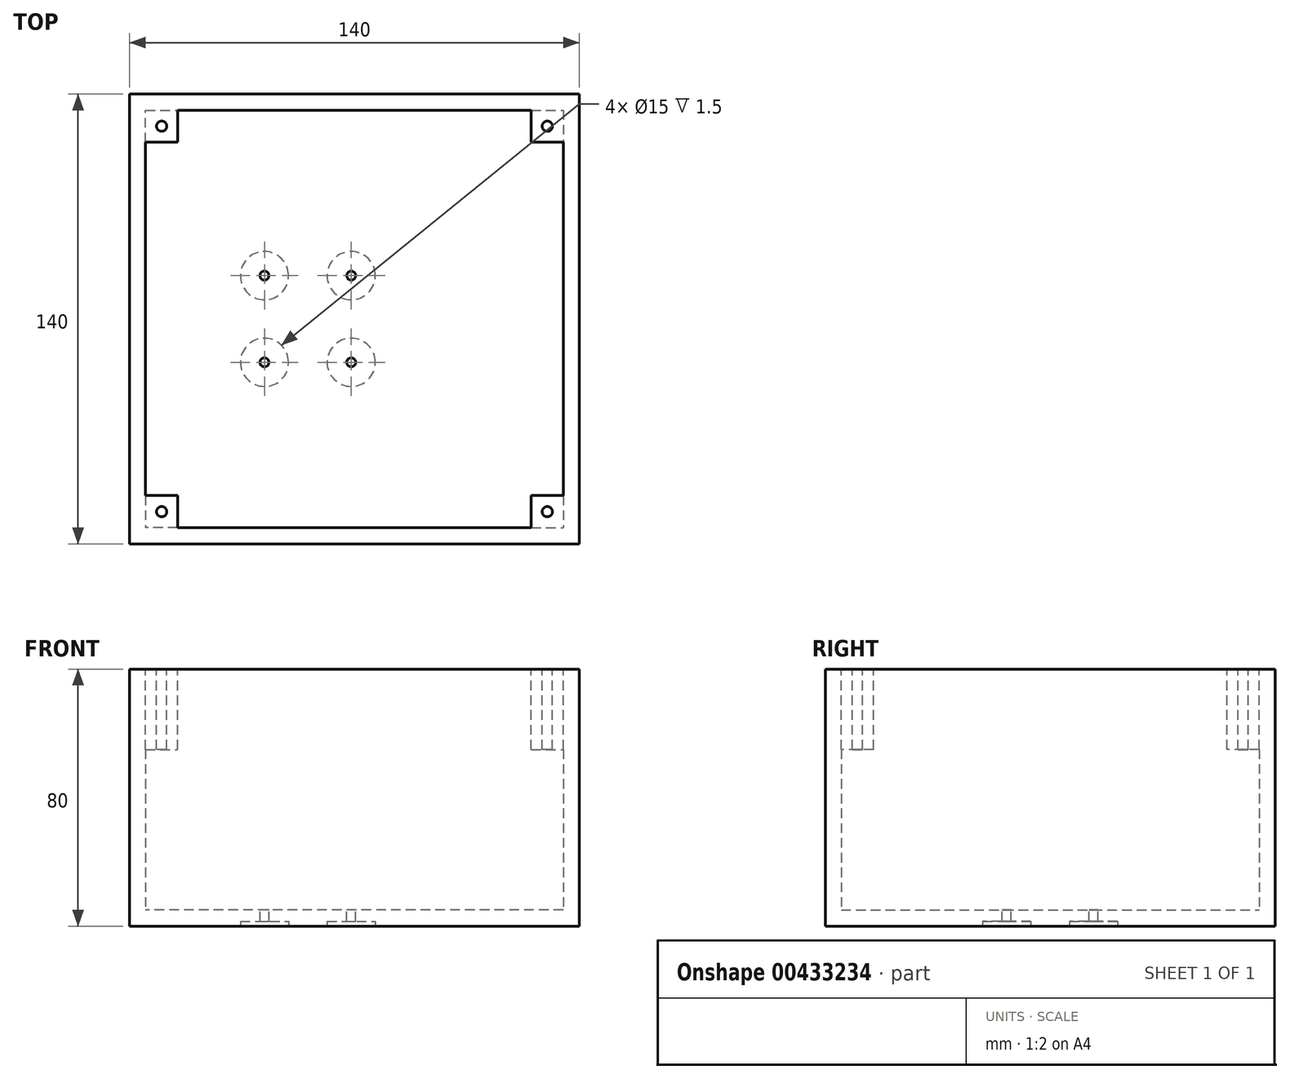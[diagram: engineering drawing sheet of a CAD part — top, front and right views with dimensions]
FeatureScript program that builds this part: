
annotation { "Feature Type Name" : "Feature", "Feature Type Description" : "" }
export const myFeature = defineFeature(function(context is Context, id is Id, definition is map)
    precondition{}
    {
        {
            var Q0;
            Q0=qCreatedBy(makeId("Top.planeOp"),FACE);
            var sketch = newSketch(context, id + "F0", { "sketchPlane" : qUnion([Q0])});
            skLineSegment(sketch, "E0.bottom", {"start": v(-70, 70) * mm, "end": v(70, 70) * mm});
            skLineSegment(sketch, "E0.top", {"start": v(-70, -70) * mm, "end": v(70, -70) * mm});
            skLineSegment(sketch, "E0.left", {"start": v(-70, 70) * mm, "end": v(-70, -70) * mm});
            skLineSegment(sketch, "E0.right", {"start": v(70, 70) * mm, "end": v(70, -70) * mm});
            skPoint(sketch, "E0.middle", {"position": v(0, 0) * mm});
            skLineSegment(sketch, "E1.bottom", {"start": v(-65, 65) * mm, "end": v(65, 65) * mm});
            skLineSegment(sketch, "E1.top", {"start": v(-65, -65) * mm, "end": v(65, -65) * mm});
            skLineSegment(sketch, "E1.left", {"start": v(-65, 65) * mm, "end": v(-65, -65) * mm});
            skLineSegment(sketch, "E1.right", {"start": v(65, 65) * mm, "end": v(65, -65) * mm});
            skSolve(sketch);
        }
        {
            var Q0;
            Q0 = qSketchRegion(id + "F0", true);
            extrude(context, id + "F1", {"entities" : qUnion([Q0]), "depth" : 80 * mm});
        }
        {
            var Q0;
            Q0=makeQuery(id+"F1.opExtrude","CAP_FACE",FACE,{"disambiguationData":[OSD([sQuery(id+"F0.wireOp",EDGE,"E0.bottom"),sQuery(id+"F0.wireOp",EDGE,"E0.top"),sQuery(id+"F0.wireOp",EDGE,"E0.left"),sQuery(id+"F0.wireOp",EDGE,"E0.right"),sQuery(id+"F0.wireOp",EDGE,"E1.bottom"),sQuery(id+"F0.wireOp",EDGE,"E1.top"),sQuery(id+"F0.wireOp",EDGE,"E1.left"),sQuery(id+"F0.wireOp",EDGE,"E1.right")])],"isStart":true});
            var sketch = newSketch(context, id + "F2", { "sketchPlane" : qUnion([Q0])});
            skLineSegment(sketch, "E2.bottom", {"start": v(-70, 70) * mm, "end": v(70, 70) * mm});
            skLineSegment(sketch, "E2.top", {"start": v(-70, -70) * mm, "end": v(70, -70) * mm});
            skLineSegment(sketch, "E2.left", {"start": v(-70, 70) * mm, "end": v(-70, -70) * mm});
            skLineSegment(sketch, "E2.right", {"start": v(70, 70) * mm, "end": v(70, -70) * mm});
            skSolve(sketch);
        }
        {
            var Q0;
            Q0 = qSketchRegion(id + "F2", true);
            extrude(context, id + "F3", {"entities" : qUnion([Q0]), "operationType" : NewBodyOperationType.ADD, "oppositeDirection" : true, "depth" : 5 * mm});
        }
        {
            var Q0;
            Q0=makeQuery(id+"F3.opExtrude","CAP_FACE",FACE,{"disambiguationData":[OSD([sQuery(id+"F2.wireOp",EDGE,"E2.bottom"),sQuery(id+"F2.wireOp",EDGE,"E2.top"),sQuery(id+"F2.wireOp",EDGE,"E2.left"),sQuery(id+"F2.wireOp",EDGE,"E2.right")])],"isStart":false});
            var sketch = newSketch(context, id + "F4", { "sketchPlane" : qUnion([Q0])});
            skLineSegment(sketch, "E3", {"start": v(0, 0) * mm, "end": v(-1, 0) * mm, "construction": true});
            skLineSegment(sketch, "E4", {"start": v(-1, 0) * mm, "end": v(-1, 13.5) * mm, "construction": true});
            skCircle(sketch, "E5", {"center": v(-1, 13.5) * mm, "radius": 1.4 * mm});
            skCircle(sketch, "E6", {"center": v(-28, 13.5) * mm, "radius": 1.4 * mm});
            skLineSegment(sketch, "E7", {"start": v(-2.4, 13.5) * mm, "end": v(-26.6, 13.5) * mm, "construction": true});
            skLineSegment(sketch, "E8.MirrorCS", {"start": v(-1, 0) * mm, "end": v(-1, -13.5) * mm, "construction": true});
            skCircle(sketch, "E9.MirrorC", {"center": v(-1, -13.5) * mm, "radius": 1.4 * mm});
            skLineSegment(sketch, "E10.MirrorCS", {"start": v(-2.4, -13.5) * mm, "end": v(-26.6, -13.5) * mm, "construction": true});
            skCircle(sketch, "E11.MirrorC", {"center": v(-28, -13.5) * mm, "radius": 1.4 * mm});
            skSolve(sketch);
        }
        {
            var Q0;
            Q0 = qSketchRegion(id + "F4", true);
            var Q1;
            Q1=makeQuery(id+"F3.boolean.opBoolean","MERGE",FACE,{"derivedFrom":[makeQuery(id+"F1.opExtrude","CAP_FACE",FACE,{"disambiguationData":[OSD([sQuery(id+"F0.wireOp",EDGE,"E0.bottom"),sQuery(id+"F0.wireOp",EDGE,"E0.top"),sQuery(id+"F0.wireOp",EDGE,"E0.left"),sQuery(id+"F0.wireOp",EDGE,"E0.right"),sQuery(id+"F0.wireOp",EDGE,"E1.bottom"),sQuery(id+"F0.wireOp",EDGE,"E1.top"),sQuery(id+"F0.wireOp",EDGE,"E1.left"),sQuery(id+"F0.wireOp",EDGE,"E1.right")])],"isStart":true}),makeQuery(id+"F3.opExtrude","CAP_FACE",FACE,{"disambiguationData":[OSD([sQuery(id+"F2.wireOp",EDGE,"E2.bottom"),sQuery(id+"F2.wireOp",EDGE,"E2.top"),sQuery(id+"F2.wireOp",EDGE,"E2.left"),sQuery(id+"F2.wireOp",EDGE,"E2.right")])],"isStart":true})]});
            extrude(context, id + "F5", {"entities" : qUnion([Q0]), "operationType" : NewBodyOperationType.REMOVE, "endBound" : BoundingType.UP_TO_SURFACE, "oppositeDirection" : true, "endBoundEntityFace" : qUnion([Q1]), "depth" : 25 * mm});
        }
        {
            var Q0;
            Q0=makeQuery(id+"F3.boolean.opBoolean","MERGE",FACE,{"derivedFrom":[makeQuery(id+"F1.opExtrude","CAP_FACE",FACE,{"disambiguationData":[OSD([sQuery(id+"F0.wireOp",EDGE,"E0.bottom"),sQuery(id+"F0.wireOp",EDGE,"E0.top"),sQuery(id+"F0.wireOp",EDGE,"E0.left"),sQuery(id+"F0.wireOp",EDGE,"E0.right"),sQuery(id+"F0.wireOp",EDGE,"E1.bottom"),sQuery(id+"F0.wireOp",EDGE,"E1.top"),sQuery(id+"F0.wireOp",EDGE,"E1.left"),sQuery(id+"F0.wireOp",EDGE,"E1.right")])],"isStart":true}),makeQuery(id+"F3.opExtrude","CAP_FACE",FACE,{"disambiguationData":[OSD([sQuery(id+"F2.wireOp",EDGE,"E2.bottom"),sQuery(id+"F2.wireOp",EDGE,"E2.top"),sQuery(id+"F2.wireOp",EDGE,"E2.left"),sQuery(id+"F2.wireOp",EDGE,"E2.right")])],"isStart":true})]});
            var sketch = newSketch(context, id + "F6", { "sketchPlane" : qUnion([Q0])});
            skCircle(sketch, "E12", {"center": v(-28, 13.5) * mm, "radius": 7.5 * mm});
            skCircle(sketch, "E13", {"center": v(-1, 13.5) * mm, "radius": 7.5 * mm});
            skCircle(sketch, "E14", {"center": v(-28, -13.5) * mm, "radius": 7.5 * mm});
            skCircle(sketch, "E15", {"center": v(-1, -13.5) * mm, "radius": 7.5 * mm});
            skSolve(sketch);
        }
        {
            var Q0;
            Q0 = qSketchRegion(id + "F6", true);
            extrude(context, id + "F7", {"entities" : qUnion([Q0]), "operationType" : NewBodyOperationType.REMOVE, "oppositeDirection" : true, "depth" : 1.5 * mm});
        }
        {
            var Q0;
            Q0=makeQuery(id+"F1.opExtrude","CAP_FACE",FACE,{"disambiguationData":[OSD([sQuery(id+"F0.wireOp",EDGE,"E0.bottom"),sQuery(id+"F0.wireOp",EDGE,"E0.top"),sQuery(id+"F0.wireOp",EDGE,"E0.left"),sQuery(id+"F0.wireOp",EDGE,"E0.right"),sQuery(id+"F0.wireOp",EDGE,"E1.bottom"),sQuery(id+"F0.wireOp",EDGE,"E1.top"),sQuery(id+"F0.wireOp",EDGE,"E1.left"),sQuery(id+"F0.wireOp",EDGE,"E1.right")])],"isStart":false});
            var sketch = newSketch(context, id + "F8", { "sketchPlane" : qUnion([Q0])});
            skLineSegment(sketch, "E16.bottom", {"start": v(-60, 60) * mm, "end": v(60, 60) * mm, "construction": true});
            skLineSegment(sketch, "E16.top", {"start": v(-60, -60) * mm, "end": v(60, -60) * mm, "construction": true});
            skLineSegment(sketch, "E16.left", {"start": v(-60, 60) * mm, "end": v(-60, -60) * mm, "construction": true});
            skLineSegment(sketch, "E16.right", {"start": v(60, 60) * mm, "end": v(60, -60) * mm, "construction": true});
            skPoint(sketch, "E16.middle", {"position": v(0, 0) * mm});
            skLineSegment(sketch, "E17.bottom", {"start": v(-65, 65) * mm, "end": v(-55, 65) * mm});
            skLineSegment(sketch, "E17.top", {"start": v(-65, 55) * mm, "end": v(-55, 55) * mm});
            skLineSegment(sketch, "E17.left", {"start": v(-65, 65) * mm, "end": v(-65, 55) * mm});
            skLineSegment(sketch, "E17.right", {"start": v(-55, 65) * mm, "end": v(-55, 55) * mm});
            skPoint(sketch, "E17.middle", {"position": v(-60, 60) * mm});
            skCircle(sketch, "E18", {"center": v(-60, 60) * mm, "radius": 1.6 * mm});
            skLineSegment(sketch, "E19.MirrorCS", {"start": v(55, 65) * mm, "end": v(55, 55) * mm});
            skLineSegment(sketch, "E20.MirrorCS", {"start": v(65, 55) * mm, "end": v(55, 55) * mm});
            skCircle(sketch, "E21.MirrorC", {"center": v(60, 60) * mm, "radius": 1.6 * mm});
            skLineSegment(sketch, "E22.MirrorCS", {"start": v(65, 65) * mm, "end": v(55, 65) * mm});
            skLineSegment(sketch, "E23.MirrorCS", {"start": v(65, 65) * mm, "end": v(65, 55) * mm});
            skLineSegment(sketch, "E24.MirrorCS", {"start": v(-65, -55) * mm, "end": v(-55, -55) * mm});
            skLineSegment(sketch, "E25.MirrorCS", {"start": v(-55, -65) * mm, "end": v(-55, -55) * mm});
            skCircle(sketch, "E26.MirrorC", {"center": v(-60, -60) * mm, "radius": 1.6 * mm});
            skLineSegment(sketch, "E27.MirrorCS", {"start": v(-65, -65) * mm, "end": v(-55, -65) * mm});
            skLineSegment(sketch, "E28.MirrorCS", {"start": v(-65, -65) * mm, "end": v(-65, -55) * mm});
            skCircle(sketch, "E29.MirrorC", {"center": v(60, -60) * mm, "radius": 1.6 * mm});
            skLineSegment(sketch, "E30.MirrorCS", {"start": v(65, -55) * mm, "end": v(55, -55) * mm});
            skLineSegment(sketch, "E31.MirrorCS", {"start": v(55, -65) * mm, "end": v(55, -55) * mm});
            skLineSegment(sketch, "E32.MirrorCS", {"start": v(65, -65) * mm, "end": v(65, -55) * mm});
            skLineSegment(sketch, "E33.MirrorCS", {"start": v(65, -65) * mm, "end": v(55, -65) * mm});
            skSolve(sketch);
        }
        {
            var Q0;
            Q0 = qSketchRegion(id + "F8", true);
            extrude(context, id + "F9", {"entities" : qUnion([Q0]), "operationType" : NewBodyOperationType.ADD, "oppositeDirection" : true, "depth" : 25 * mm});
        }
    });
